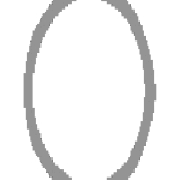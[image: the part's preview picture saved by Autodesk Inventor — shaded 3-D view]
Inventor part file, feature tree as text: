
AUTODESK INVENTOR PART (.ipt)
format: ipt  version: 2021 (Build 250183000, 183)  size: 114,688 bytes
history: native  units: in
note: dims shown in document units (in); Inventor stores cm internally (conversion verified against a paired STEP export)
features: other x4, sketch x3, plane x1
ambient origin geometry x8: Origin, YZ Plane, XZ Plane, XY Plane, X Axis, Y Axis, Z Axis, Center Point
bodies: Solid1 (feature_tree), Body (feature_tree)
feature tree (8):
  other  "Driven Length"
  other  "Frame Generator"
  other  "Start Plane"
  other  "End Plane"
  sketch  "Sketch"  dims[d2=2.0in d4=-0.0in d5=2.0in d6=0.12in d7=0.0in d8=90.0deg d9=2.0in]
  sketch  "Sketch2"  dims[d0=1.0in]
  plane  "Work Plane3"
  sketch  "Sketch3"  dims[d1=0.065in]
